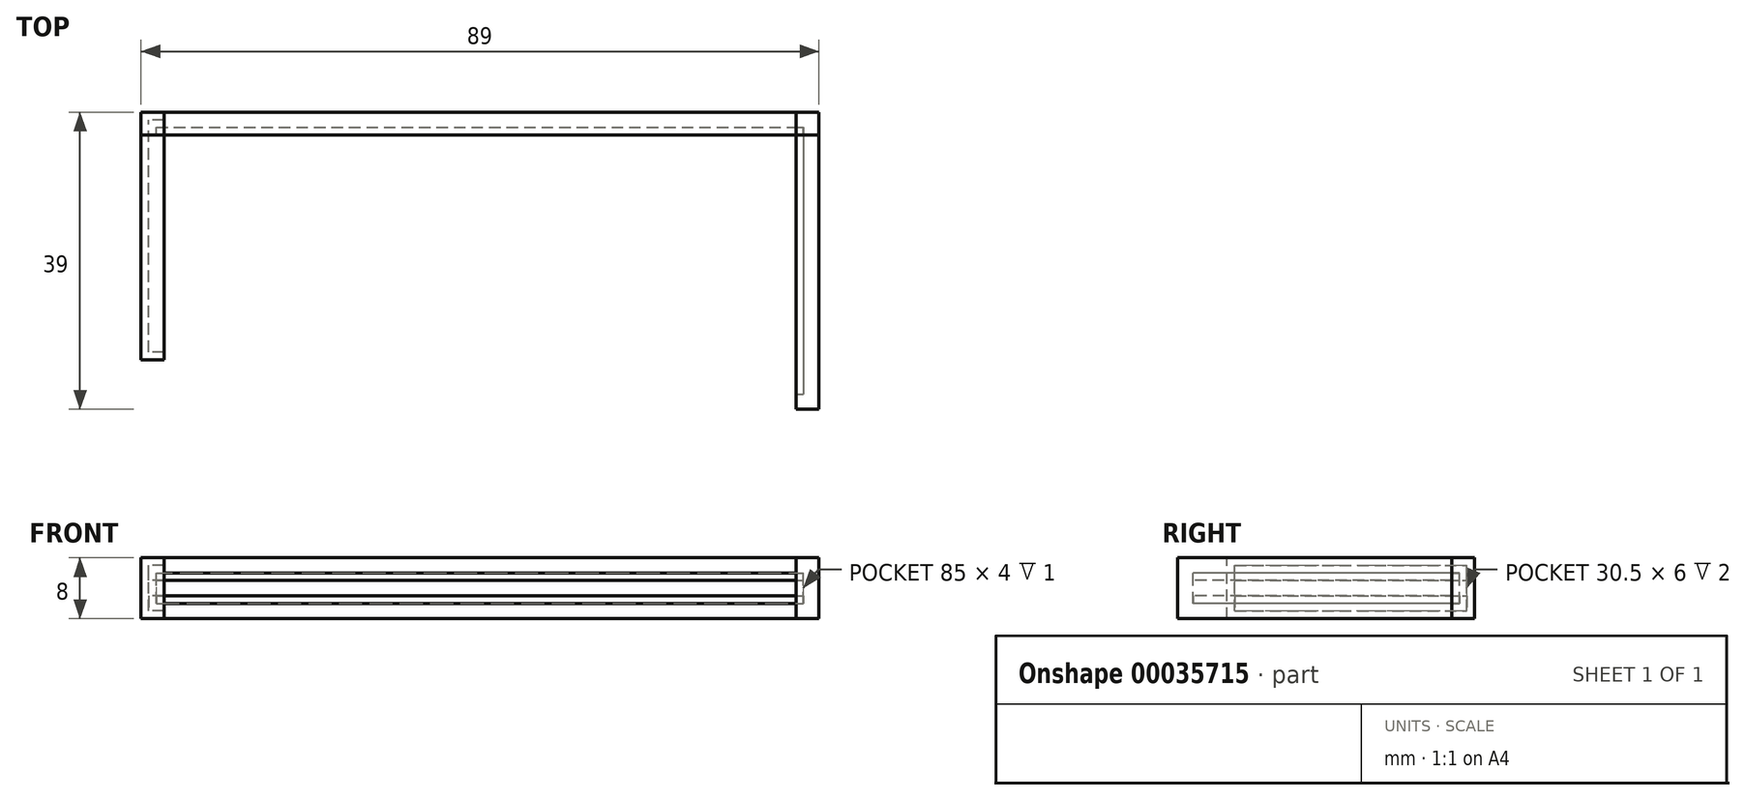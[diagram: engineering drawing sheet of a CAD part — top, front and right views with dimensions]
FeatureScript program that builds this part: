
annotation { "Feature Type Name" : "Feature", "Feature Type Description" : "" }
export const myFeature = defineFeature(function(context is Context, id is Id, definition is map)
    precondition{}
    {
        {
            var Q0;
            Q0=qCreatedBy(makeId("Top.planeOp"),FACE);
            var sketch = newSketch(context, id + "F0", { "sketchPlane" : qUnion([Q0])});
            skLineSegment(sketch, "E0.rect.bottom", {"start": v(-44.5, 28.5) * mm, "end": v(44.5, 28.5) * mm});
            skLineSegment(sketch, "E0.rect.left", {"start": v(-44.5, 28.5) * mm, "end": v(-44.5, -4) * mm});
            skLineSegment(sketch, "E0.rect.right", {"start": v(44.5, 28.5) * mm, "end": v(44.5, -10.5) * mm});
            skPoint(sketch, "E0.rect.middle", {"position": v(0, 0) * mm});
            skSolve(sketch);
        }
        {
            var Q0;
            Q0=sQuery(id+"F0.wireOp",EDGE,"E0.rect.bottom");
            var Q1;
            Q1=sQuery(id+"F0.wireOp",EDGE,"E0.rect.left");
            var Q2;
            Q2=sQuery(id+"F0.wireOp",EDGE,"E0.rect.right");
            extrude(context, id + "F1", {"bodyType" : ToolBodyType.SURFACE, "surfaceEntities" : qUnion([Q0, Q1, Q2]), "depth" : 8 * mm});
        }
        {
            var Q0;
            Q0=makeQuery(id+"F1.opExtrude","SWEPT_FACE",FACE,{"disambiguationData":[OSD([sQuery(id+"F0.wireOp",EDGE,"E0.rect.left")])]});
            extrude(context, id + "F2", {"entities" : qUnion([Q0]), "depth" : 3 * mm});
        }
        {
            var Q0;
            Q0=makeQuery(id+"F1.opExtrude","SWEPT_FACE",FACE,{"disambiguationData":[OSD([sQuery(id+"F0.wireOp",EDGE,"E0.rect.right")])]});
            extrude(context, id + "F3", {"entities" : qUnion([Q0]), "depth" : 3 * mm});
        }
        {
            var Q0;
            Q0=makeQuery(id+"F1.opExtrude","SWEPT_FACE",FACE,{"disambiguationData":[OSD([sQuery(id+"F0.wireOp",EDGE,"E0.rect.bottom")])]});
            extrude(context, id + "F4", {"entities" : qUnion([Q0]), "depth" : 3 * mm});
        }
        {
            var Q0;
            Q0=makeQuery(id+"F4.opExtrude","CAP_FACE",FACE,{"disambiguationData":[OSD([sQuery(id+"F0.wireOp",EDGE,"E0.rect.bottom")])],"isStart":false});
            shell(context, id + "F5", {"entities" : qUnion([Q0]), "thickness" : 2 * mm});
        }
        {
            var Q0;
            {var subQ0=sQuery(id+"F0.wireOp",EDGE,"E0.rect.bottom");Q0=makeQuery(id+"F5.opShell","OFFSET_FACE",FACE,{"disambiguationData":[OSD([subQ0]),TDD([makeQuery(id+"F4.opExtrude","SWEPT_FACE",FACE,{"disambiguationData":[OSD([subQ0]),TDD([makeQuery(id+"F1.opExtrude","CAP_EDGE",EDGE,{"disambiguationData":[OSD([subQ0])],"isStart":true})])]})])]});}
            extrude(context, id + "F6", {"entities" : qUnion([Q0]), "depth" : 1 * mm});
        }
        {
            var Q0;
            {var subQ0=sQuery(id+"F0.wireOp",EDGE,"E0.rect.bottom");Q0=makeQuery(id+"F5.opShell","OFFSET_FACE",FACE,{"disambiguationData":[OSD([subQ0]),TDD([makeQuery(id+"F4.opExtrude","SWEPT_FACE",FACE,{"disambiguationData":[OSD([subQ0]),TDD([makeQuery(id+"F1.opExtrude","CAP_EDGE",EDGE,{"disambiguationData":[OSD([subQ0])],"isStart":false})])]})])]});}
            extrude(context, id + "F7", {"entities" : qUnion([Q0]), "depth" : 1 * mm});
        }
        {
            var Q0;
            Q0=makeQuery(id+"F2.opExtrude","CAP_FACE",FACE,{"disambiguationData":[OSD([sQuery(id+"F0.wireOp",EDGE,"E0.rect.left")])],"isStart":false});
            shell(context, id + "F8", {"entities" : qUnion([Q0]), "thickness" : 1 * mm});
        }
        {
            var Q0;
            {var subQ0=sQuery(id+"F0.wireOp",EDGE,"E0.rect.left");Q0=makeQuery(id+"F8.opShell","OFFSET_FACE",FACE,{"disambiguationData":[OSD([subQ0]),TDD([makeQuery(id+"F2.opExtrude","SWEPT_FACE",FACE,{"disambiguationData":[OSD([subQ0]),TDD([makeQuery(id+"F1.opExtrude","CAP_EDGE",EDGE,{"disambiguationData":[OSD([subQ0])],"isStart":true})])]})])]});}
            extrude(context, id + "F9", {"entities" : qUnion([Q0]), "depth" : 2 * mm});
        }
        {
            var Q0;
            {var subQ0=sQuery(id+"F0.wireOp",EDGE,"E0.rect.left");Q0=makeQuery(id+"F8.opShell","OFFSET_FACE",FACE,{"disambiguationData":[OSD([subQ0]),TDD([makeQuery(id+"F2.opExtrude","SWEPT_FACE",FACE,{"disambiguationData":[OSD([subQ0]),TDD([makeQuery(id+"F1.opExtrude","CAP_EDGE",EDGE,{"disambiguationData":[OSD([subQ0])],"isStart":false})])]})])]});}
            extrude(context, id + "F10", {"entities" : qUnion([Q0]), "depth" : 2 * mm});
        }
        {
            var Q0;
            Q0=makeQuery(id+"F3.opExtrude","CAP_FACE",FACE,{"disambiguationData":[OSD([sQuery(id+"F0.wireOp",EDGE,"E0.rect.right")])],"isStart":false});
            shell(context, id + "F11", {"entities" : qUnion([Q0]), "thickness" : 2 * mm});
        }
        {
            var Q0;
            {var subQ0=sQuery(id+"F0.wireOp",EDGE,"E0.rect.right");Q0=makeQuery(id+"F11.opShell","OFFSET_FACE",FACE,{"disambiguationData":[OSD([subQ0]),TDD([makeQuery(id+"F3.opExtrude","SWEPT_FACE",FACE,{"disambiguationData":[OSD([subQ0]),TDD([makeQuery(id+"F1.opExtrude","CAP_EDGE",EDGE,{"disambiguationData":[OSD([subQ0])],"isStart":true})])]})])]});}
            var sketch = newSketch(context, id + "F12", { "sketchPlane" : qUnion([Q0])});
            skLineSegment(sketch, "E1", {"start": v(41.5, 25.5) * mm, "end": v(42.5, 25.5) * mm});
            skSolve(sketch);
        }
        {
            var Q0;
            {var subQ3=sQuery(id+"F12.wireOp",EDGE,"E1");Q0=makeQuery(id+"F12.imprint","IMPRINT",FACE,{"disambiguationData":[TD([[makeQuery(id+"F12.imprint","IMPRINT",EDGE,{"derivedFrom":subQ3}),-1.0]])]});}
            extrude(context, id + "F13", {"entities" : qUnion([Q0]), "depth" : 1 * mm});
        }
        {
            var Q0;
            {var subQ0=sQuery(id+"F0.wireOp",EDGE,"E0.rect.right");Q0=makeQuery(id+"F11.opShell","OFFSET_FACE",FACE,{"disambiguationData":[OSD([subQ0]),TDD([makeQuery(id+"F3.opExtrude","SWEPT_FACE",FACE,{"disambiguationData":[OSD([subQ0]),TDD([makeQuery(id+"F1.opExtrude","CAP_EDGE",EDGE,{"disambiguationData":[OSD([subQ0])],"isStart":false})])]})])]});}
            var sketch = newSketch(context, id + "F14", { "sketchPlane" : qUnion([Q0])});
            skLineSegment(sketch, "E2", {"start": v(41.5, -25.5) * mm, "end": v(42.5, -25.5) * mm});
            skSolve(sketch);
        }
        {
            var Q0;
            {var subQ3=sQuery(id+"F14.wireOp",EDGE,"E2");Q0=makeQuery(id+"F14.imprint","IMPRINT",FACE,{"disambiguationData":[TD([[makeQuery(id+"F14.imprint","IMPRINT",EDGE,{"derivedFrom":subQ3}),1.0]])]});}
            extrude(context, id + "F15", {"entities" : qUnion([Q0]), "depth" : 1 * mm});
        }
    });
